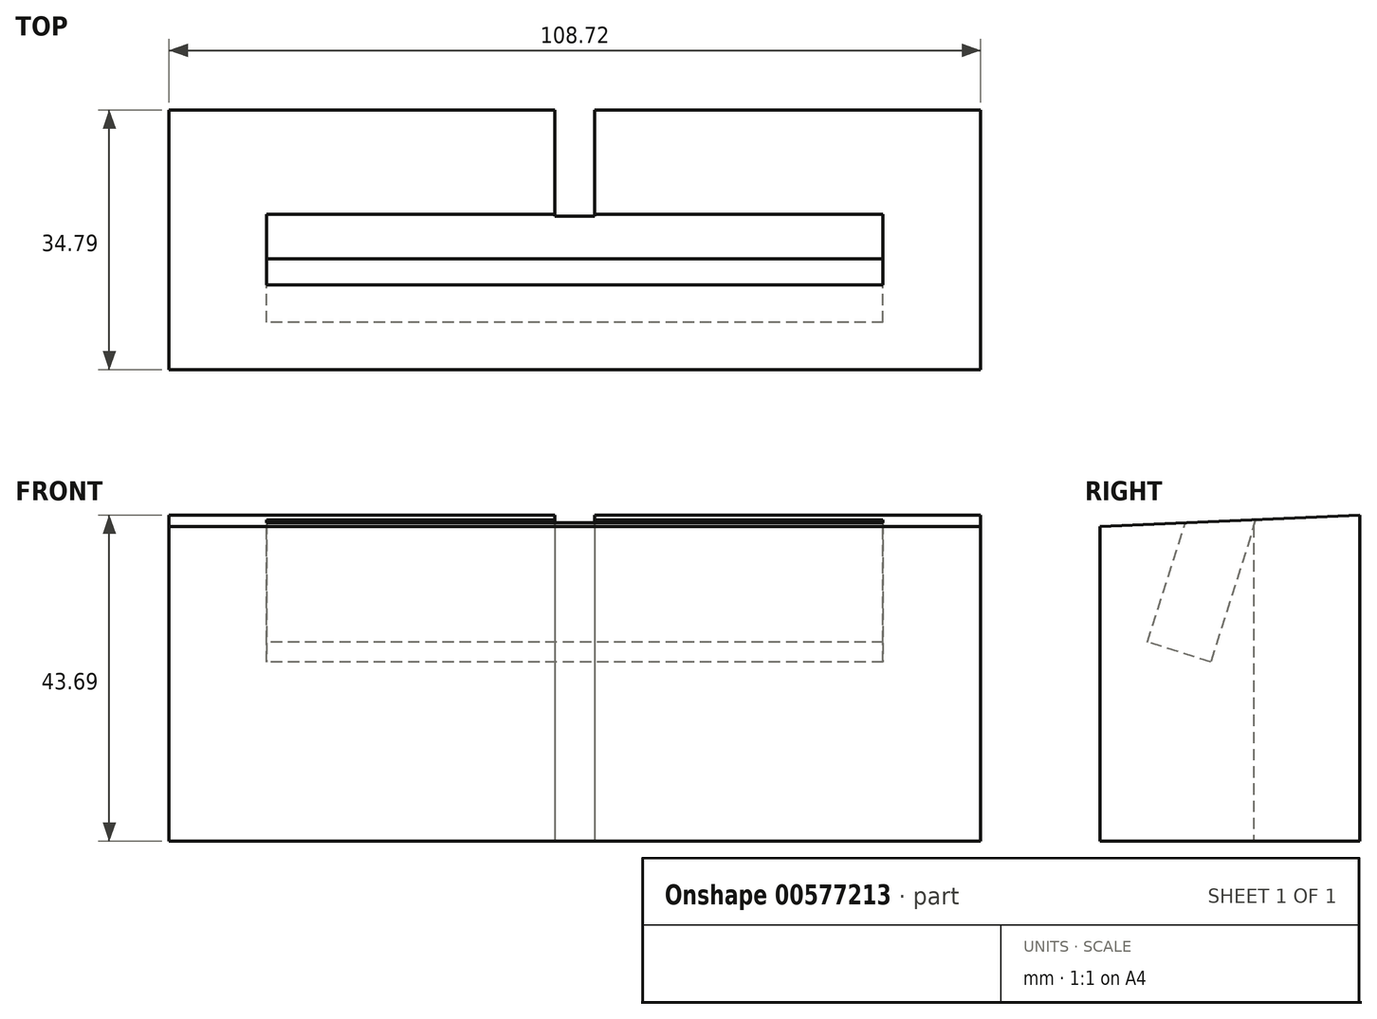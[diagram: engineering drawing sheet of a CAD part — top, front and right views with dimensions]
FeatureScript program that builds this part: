
annotation { "Feature Type Name" : "Feature", "Feature Type Description" : "" }
export const myFeature = defineFeature(function(context is Context, id is Id, definition is map)
    precondition{}
    {
        {
            var Q0;
            Q0=qCreatedBy(makeId("Top.planeOp"),FACE);
            var sketch = newSketch(context, id + "F0", { "sketchPlane" : qUnion([Q0])});
            skLineSegment(sketch, "E0.bottom", {"start": v(-54.36, -23.55) * mm, "end": v(54.36, -23.55) * mm});
            skLineSegment(sketch, "E0.top", {"start": v(-54.36, 11.24) * mm, "end": v(54.36, 11.24) * mm});
            skLineSegment(sketch, "E0.left", {"start": v(-54.36, -23.55) * mm, "end": v(-54.36, 11.24) * mm});
            skLineSegment(sketch, "E0.right", {"start": v(54.36, -23.55) * mm, "end": v(54.36, 11.24) * mm});
            skSolve(sketch);
        }
        {
            var Q0;
            Q0=makeQuery(id+"F0.imprint","IMPRINT",FACE,{"disambiguationData":[TD([[makeQuery(id+"F0.imprint","IMPRINT",EDGE,{"derivedFrom":sQuery(id+"F0.wireOp",EDGE,"E0.bottom")}),1.0]])]});
            extrude(context, id + "F1", {"entities" : qUnion([Q0]), "depth" : 43.69 * mm, "offsetDistance" : 25.4 * mm});
        }
        {
            var Q0;
            Q0=makeQuery(id+"F1.opExtrude","SWEPT_FACE",FACE,{"disambiguationData":[OSD([sQuery(id+"F0.wireOp",EDGE,"E0.right")])]});
            var sketch = newSketch(context, id + "F2", { "sketchPlane" : qUnion([Q0])});
            skLineSegment(sketch, "E1", {"start": v(11.24, 43.69) * mm, "end": v(-23.55, 42.16) * mm});
            skLineSegment(sketch, "E2", {"start": v(-23.55, 42.16) * mm, "end": v(-23.55, 43.69) * mm});
            skLineSegment(sketch, "E3", {"start": v(-23.55, 43.69) * mm, "end": v(11.24, 43.69) * mm});
            skSolve(sketch);
        }
        {
            var Q0;
            Q0 = qSketchRegion(id + "F2", true);
            extrude(context, id + "F3", {"entities" : qUnion([Q0]), "operationType" : NewBodyOperationType.REMOVE, "endBound" : BoundingType.THROUGH_ALL, "oppositeDirection" : true, "depth" : 25.4 * mm, "offsetDistance" : 25.4 * mm});
        }
        {
            var Q0;
            Q0=makeQuery(id+"F1.opExtrude","SWEPT_FACE",FACE,{"disambiguationData":[OSD([sQuery(id+"F0.wireOp",EDGE,"E0.top")])]});
            var sketch = newSketch(context, id + "F4", { "sketchPlane" : qUnion([Q0])});
            skLineSegment(sketch, "E4.bottom", {"start": v(-2.67, 43.69) * mm, "end": v(2.67, 43.69) * mm});
            skLineSegment(sketch, "E4.top", {"start": v(-2.67, 0) * mm, "end": v(2.67, 0) * mm});
            skLineSegment(sketch, "E4.left", {"start": v(-2.67, 43.69) * mm, "end": v(-2.67, 0) * mm});
            skLineSegment(sketch, "E4.right", {"start": v(2.67, 43.69) * mm, "end": v(2.67, 0) * mm});
            skSolve(sketch);
        }
        {
            var Q0;
            Q0 = qSketchRegion(id + "F4", true);
            extrude(context, id + "F5", {"entities" : qUnion([Q0]), "operationType" : NewBodyOperationType.REMOVE, "oppositeDirection" : true, "depth" : 14.22 * mm, "offsetDistance" : 25.4 * mm});
        }
        {
            var Q0;
            Q0=qCreatedBy(makeId("Right.planeOp"),FACE);
            var sketch = newSketch(context, id + "F6", { "sketchPlane" : qUnion([Q0])});
            skLineSegment(sketch, "E5", {"start": v(3.65, 63.27) * mm, "end": v(-8.72, 24) * mm});
            skLineSegment(sketch, "E6", {"start": v(-8.72, 24) * mm, "end": v(-17.2, 26.67) * mm});
            skLineSegment(sketch, "E7", {"start": v(-17.2, 26.67) * mm, "end": v(-5.82, 62.8) * mm});
            skLineSegment(sketch, "E8", {"start": v(-5.82, 62.8) * mm, "end": v(3.65, 63.27) * mm});
            skSolve(sketch);
        }
        {
            var Q0;
            Q0 = qSketchRegion(id + "F6", true);
            extrude(context, id + "F7", {"entities" : qUnion([Q0]), "operationType" : NewBodyOperationType.REMOVE, "depth" : 41.27 * mm, "offsetDistance" : 25.4 * mm, "hasSecondDirection" : true, "secondDirectionOppositeDirection" : true, "secondDirectionDepth" : 41.27 * mm});
        }
    });
